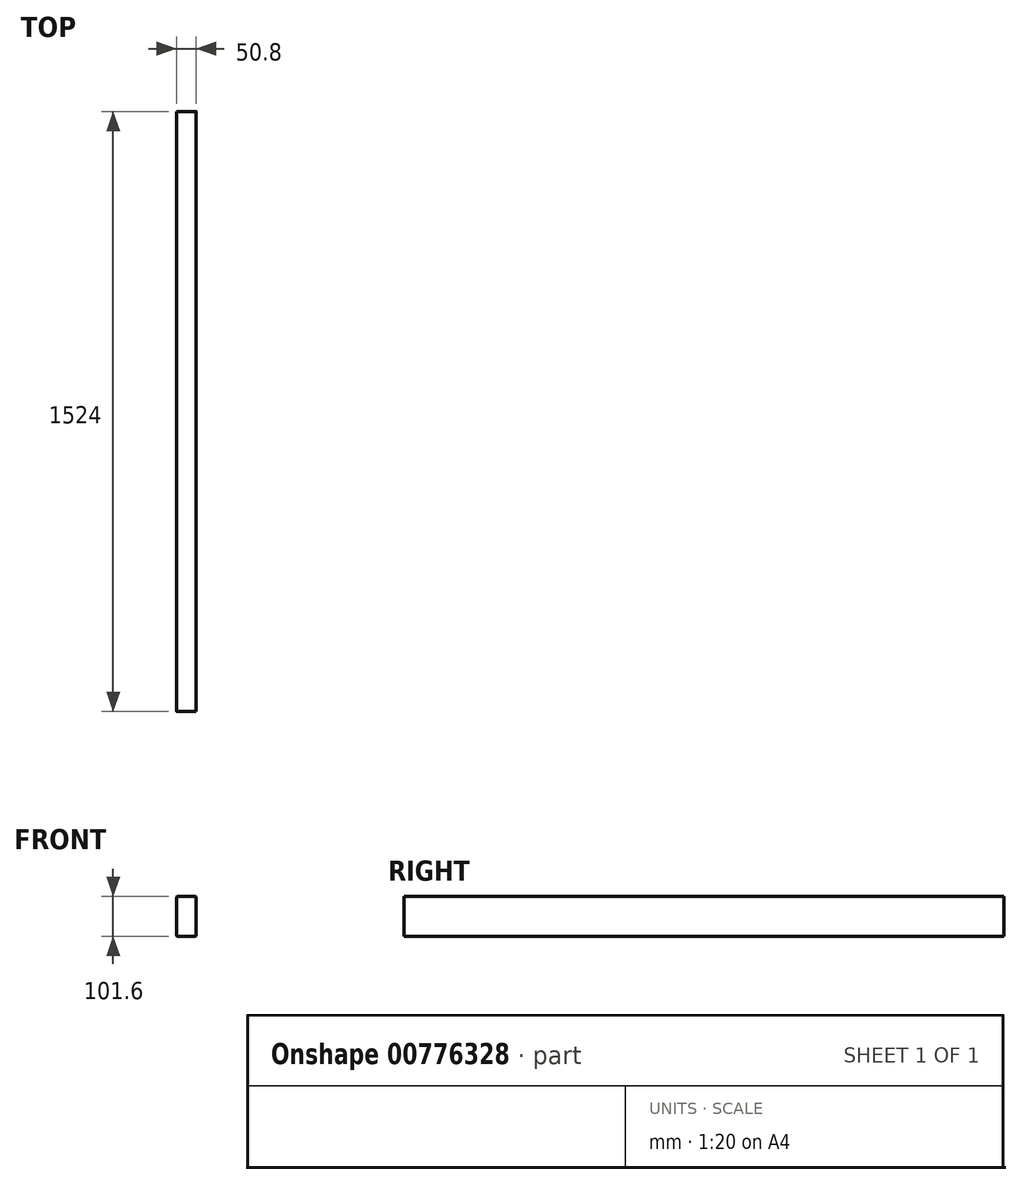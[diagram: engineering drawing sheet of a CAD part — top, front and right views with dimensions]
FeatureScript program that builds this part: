
annotation { "Feature Type Name" : "Feature", "Feature Type Description" : "" }
export const myFeature = defineFeature(function(context is Context, id is Id, definition is map)
    precondition{}
    {
        {
            var Q0;
            Q0=qCreatedBy(makeId("Top.planeOp"),FACE);
            var sketch = newSketch(context, id + "F0", { "sketchPlane" : qUnion([Q0])});
            skLineSegment(sketch, "E0.bottom", {"start": v(25.4, 762) * mm, "end": v(-25.4, 762) * mm});
            skLineSegment(sketch, "E0.top", {"start": v(25.4, -762) * mm, "end": v(-25.4, -762) * mm});
            skLineSegment(sketch, "E0.left", {"start": v(25.4, 762) * mm, "end": v(25.4, -762) * mm});
            skLineSegment(sketch, "E0.right", {"start": v(-25.4, 762) * mm, "end": v(-25.4, -762) * mm});
            skPoint(sketch, "E0.middle", {"position": v(0, 0) * mm});
            skSolve(sketch);
        }
        {
            var Q0;
            Q0=makeQuery(id+"F0.imprint","IMPRINT",FACE,{"disambiguationData":[TD([[makeQuery(id+"F0.imprint","IMPRINT",EDGE,{"derivedFrom":sQuery(id+"F0.wireOp",EDGE,"E0.bottom")}),1.0]])]});
            extrude(context, id + "F1", {"entities" : qUnion([Q0]), "endBound" : BoundingType.SYMMETRIC, "depth" : 101.6 * mm, "offsetDistance" : 25.4 * mm});
        }
        {
            var Q0;
            Q0=makeQuery(id+"F1.opExtrude","CAP_EDGE",EDGE,{"disambiguationData":[OSD([sQuery(id+"F0.wireOp",EDGE,"E0.left")])],"isStart":false});
            var Q1;
            Q1=makeQuery(id+"F1.opExtrude","CAP_EDGE",EDGE,{"disambiguationData":[OSD([sQuery(id+"F0.wireOp",EDGE,"E0.right")])],"isStart":false});
            var Q2;
            Q2=makeQuery(id+"F1.opExtrude","CAP_EDGE",EDGE,{"disambiguationData":[OSD([sQuery(id+"F0.wireOp",EDGE,"E0.left")])],"isStart":true});
            var Q3;
            Q3=makeQuery(id+"F1.opExtrude","CAP_EDGE",EDGE,{"disambiguationData":[OSD([sQuery(id+"F0.wireOp",EDGE,"E0.right")])],"isStart":true});
            fillet(context, id + "F2", {"entities" : qUnion([Q0, Q1, Q2, Q3]), "radius" : 3.17 * mm, "tangentPropagation" : true, "allowEdgeOverflow" : false});
        }
        {
            var Q0;
            Q0=makeQuery(id+"F1.opExtrude","SWEPT_BODY",BODY,{"disambiguationData":[OSD([sQuery(id+"F0.wireOp",EDGE,"E0.bottom"),sQuery(id+"F0.wireOp",EDGE,"E0.top"),sQuery(id+"F0.wireOp",EDGE,"E0.left"),sQuery(id+"F0.wireOp",EDGE,"E0.right")])]});
            transform(context, id + "F3", {"entities" : qUnion([Q0]), "transformType" : TransformType.TRANSLATION_3D, "dx" : 0 * mm, "dy" : 0 * mm, "dz" : 0 * mm, "makeCopy" : true});
        }
    });
